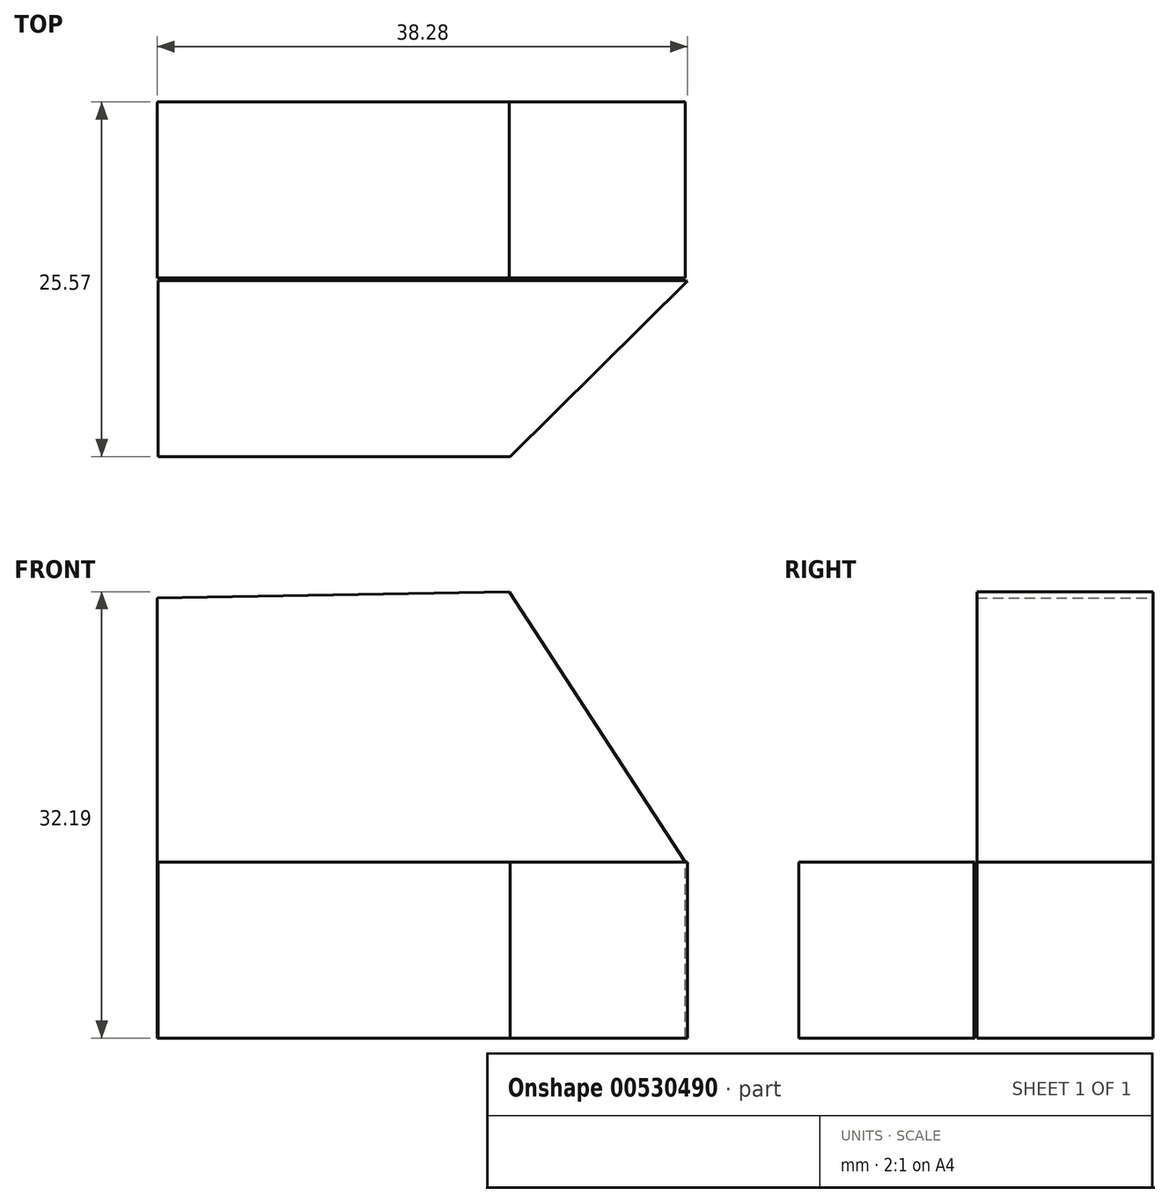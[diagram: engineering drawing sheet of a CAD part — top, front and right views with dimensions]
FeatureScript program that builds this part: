
annotation { "Feature Type Name" : "Feature", "Feature Type Description" : "" }
export const myFeature = defineFeature(function(context is Context, id is Id, definition is map)
    precondition{}
    {
        {
            var Q0;
            Q0=qCreatedBy(makeId("Front.planeOp"),FACE);
            var sketch = newSketch(context, id + "F0", { "sketchPlane" : qUnion([Q0])});
            skLineSegment(sketch, "E0", {"start": v(-61.64, 31.75) * mm, "end": v(-61.64, 0) * mm});
            skLineSegment(sketch, "E1", {"start": v(-61.64, 0) * mm, "end": v(-23.54, 0) * mm});
            skLineSegment(sketch, "E2", {"start": v(-23.54, 0) * mm, "end": v(-23.54, 12.7) * mm});
            skLineSegment(sketch, "E3", {"start": v(-23.54, 12.7) * mm, "end": v(-36.24, 32.19) * mm});
            skLineSegment(sketch, "E4", {"start": v(-36.24, 32.19) * mm, "end": v(-61.64, 31.75) * mm});
            skSolve(sketch);
        }
        {
            var Q0;
            Q0 = qSketchRegion(id + "F0", true);
            extrude(context, id + "F1", {"entities" : qUnion([Q0]), "depth" : 12.7 * mm, "offsetDistance" : 25.4 * mm});
        }
        {
            var Q0;
            Q0=qCreatedBy(makeId("Top.planeOp"),FACE);
            var sketch = newSketch(context, id + "F2", { "sketchPlane" : qUnion([Q0])});
            skLineSegment(sketch, "E5", {"start": v(-61.56, -12.87) * mm, "end": v(-61.56, -25.57) * mm});
            skLineSegment(sketch, "E6", {"start": v(-61.56, -25.57) * mm, "end": v(-36.16, -25.57) * mm});
            skLineSegment(sketch, "E7", {"start": v(-23.36, -12.91) * mm, "end": v(-36.16, -25.57) * mm});
            skLineSegment(sketch, "E8", {"start": v(-23.36, -12.91) * mm, "end": v(-61.56, -12.87) * mm});
            skSolve(sketch);
        }
        {
            var Q0;
            Q0=makeQuery(id+"F2.imprint","IMPRINT",FACE,{"disambiguationData":[TD([[makeQuery(id+"F2.imprint","IMPRINT",EDGE,{"derivedFrom":sQuery(id+"F2.wireOp",EDGE,"E5")}),1.0]])]});
            extrude(context, id + "F3", {"entities" : qUnion([Q0]), "operationType" : NewBodyOperationType.ADD, "depth" : 12.7 * mm, "offsetDistance" : 25.4 * mm});
        }
    });
